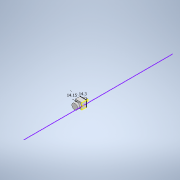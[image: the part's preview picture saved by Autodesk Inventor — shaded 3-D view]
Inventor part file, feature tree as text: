
AUTODESK INVENTOR PART (.ipt)
format: ipt  version: 2020 (Build 240168000, 168)  size: 212,992 bytes
history: native  units: mm
features: extrude x12, sketch x9, projected_geometry x7, plane x1, fillet x1
ambient origin geometry x8: Origin, YZ Plane, XZ Plane, XY Plane, X Axis, Y Axis, Z Axis, Center Point
bodies: Solid1 (feature_tree)
feature tree (30):
  extrude  "Extrusion1"  Depth=14.3mm
  sketch  "Sketch2"  dims[d2=8.0mm d3=0.0mm d4=10.75mm]
  extrude  "Extrusion2"  Depth=10.75mm
  extrude  "Extrusion3"  Depth=8.0mm TaperAngle=0.0deg
  plane  "Work Plane1"
  sketch  "Sketch3"  dims[d5=2.0mm d6=8.0mm d7=0.0mm]
  extrude  "Extrusion4"  Depth=12.3mm
  extrude  "Extrusion5"  Depth=8.0mm TaperAngle=0.0deg
  extrude  "Extrusion6"  Depth=14.5mm
  extrude  "Extrusion7"  Depth=13.1mm
  extrude  "Extrusion8"  Depth=19.3mm
  extrude  "Extrusion9"  Depth=3.55mm
  fillet  "Fillet1"  Radius=8.35mm
  extrude  "Extrusion10"  Depth=3.45mm
  extrude  "Extrusion11"  Depth=3.55mm TaperAngle=0.0deg
  extrude  "Extrusion12"  Depth=3.55mm TaperAngle=0.0deg
  sketch  "Sketch9"  dims[d24=0.0mm d25=0.0mm d26=5.0mm d28=8.35mm d29=3.45mm d30=3.55mm d31=0.0mm d32=3.55mm d33=0.0mm d34=3.55mm d35=0.0mm]
  sketch  "Sketch1"  dims[d0=14.15mm d1=14.3mm]
  projected_geometry  "Projected Loop1"
  projected_geometry  "Projected Loop2"
  projected_geometry  "Projected Loop3"
  projected_geometry  "Projected Loop4"
  sketch  "Sketch4"  dims[d8=8.0mm d9=0.0mm d10=12.3mm]
  sketch  "Sketch5"  dims[d11=8.0mm d12=0.0mm d13=8.0mm d14=0.0mm]
  sketch  "Sketch6"  dims[d15=8.0mm d16=0.0mm d17=14.5mm]
  projected_geometry  "Projected Loop5"
  sketch  "Sketch7"  dims[d18=0.0mm d19=0.0mm d20=13.1mm]
  projected_geometry  "Projected Loop6"
  sketch  "Sketch8"  dims[d21=8.0mm d22=0.0mm d23=19.3mm]
  projected_geometry  "Projected Loop7"
